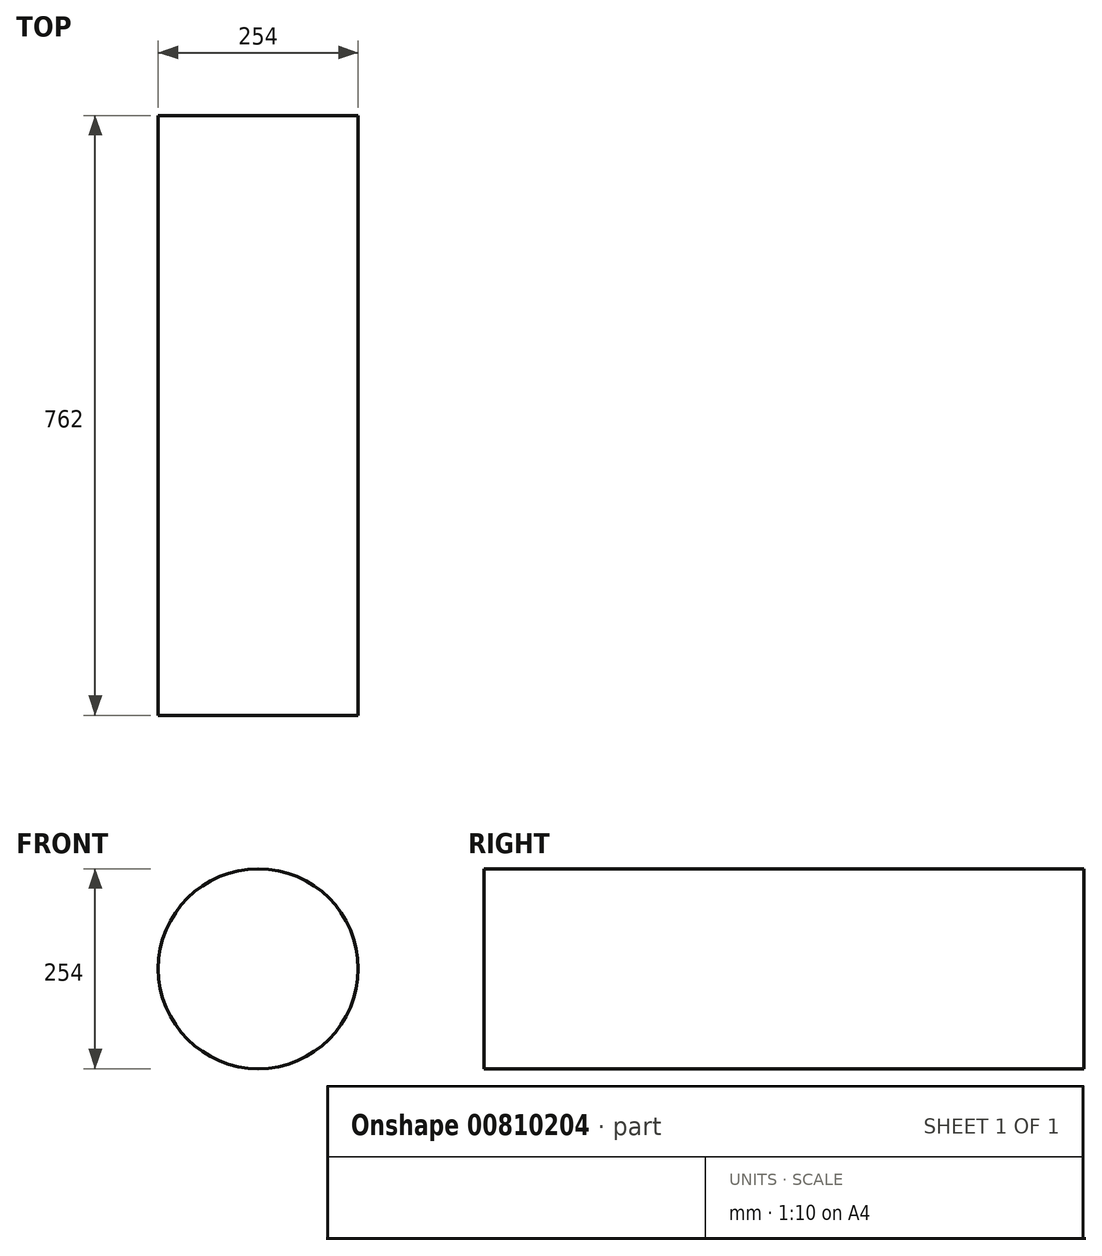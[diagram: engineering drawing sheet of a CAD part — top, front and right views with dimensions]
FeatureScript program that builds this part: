
annotation { "Feature Type Name" : "Feature", "Feature Type Description" : "" }
export const myFeature = defineFeature(function(context is Context, id is Id, definition is map)
    precondition{}
    {
        {
            var Q0;
            Q0=qCreatedBy(makeId("Front.planeOp"),FACE);
            var sketch = newSketch(context, id + "F0", { "sketchPlane" : qUnion([Q0])});
            skCircle(sketch, "E0", {"center": v(0, 0) * mm, "radius": 64.38 * mm});
            skCircle(sketch, "E1", {"center": v(0, 0) * mm, "radius": 127 * mm});
            skSolve(sketch);
        }
        {
            var Q0;
            Q0=makeQuery(id+"F0.imprint","IMPRINT",FACE,{"disambiguationData":[TD([[makeQuery(id+"F0.imprint","IMPRINT",EDGE,{"derivedFrom":sQuery(id+"F0.wireOp",EDGE,"E0")}),1.0]])]});
            var Q1;
            Q1=makeQuery(id+"F0.imprint","IMPRINT",FACE,{"disambiguationData":[TD([[makeQuery(id+"F0.imprint","IMPRINT",EDGE,{"derivedFrom":sQuery(id+"F0.wireOp",EDGE,"E0")}),-1.0]])]});
            extrude(context, id + "F1", {"entities" : qUnion([Q0, Q1]), "endBound" : BoundingType.SYMMETRIC, "depth" : 762 * mm, "offsetDistance" : 25.4 * mm});
        }
    });
